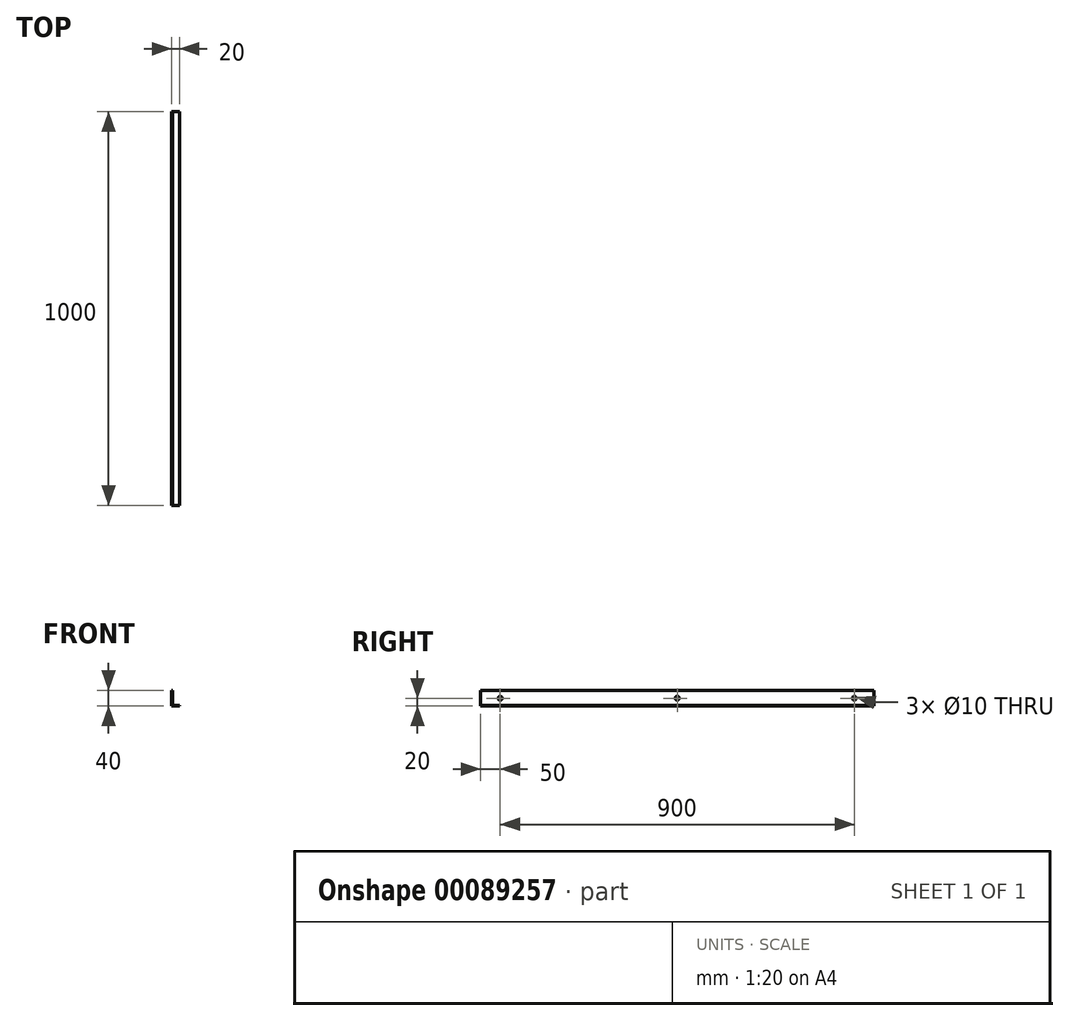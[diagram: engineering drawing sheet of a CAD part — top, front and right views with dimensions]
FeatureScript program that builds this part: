
annotation { "Feature Type Name" : "Feature", "Feature Type Description" : "" }
export const myFeature = defineFeature(function(context is Context, id is Id, definition is map)
    precondition{}
    {
        {
            var Q0;
            Q0=qCreatedBy(makeId("Front.planeOp"),FACE);
            var sketch = newSketch(context, id + "F0", { "sketchPlane" : qUnion([Q0])});
            skLineSegment(sketch, "E0.bottom", {"start": v(-8, 1) * mm, "end": v(10, 1) * mm});
            skLineSegment(sketch, "E0.top", {"start": v(-10, -1) * mm, "end": v(10, -1) * mm});
            skLineSegment(sketch, "E0.left", {"start": v(-10, 1) * mm, "end": v(-10, -1) * mm});
            skLineSegment(sketch, "E0.right", {"start": v(10, 1) * mm, "end": v(10, -1) * mm});
            skPoint(sketch, "E0.middle", {"position": v(0, 0) * mm});
            skLineSegment(sketch, "E1.bottom", {"start": v(-10, -1) * mm, "end": v(-8, -1) * mm});
            skLineSegment(sketch, "E1.top", {"start": v(-10, 39) * mm, "end": v(-8, 39) * mm});
            skLineSegment(sketch, "E1.left", {"start": v(-10, -1) * mm, "end": v(-10, 39) * mm});
            skLineSegment(sketch, "E1.right", {"start": v(-8, 1) * mm, "end": v(-8, 39) * mm});
            skSolve(sketch);
        }
        {
            var Q0;
            Q0 = qSketchRegion(id + "F0", true);
            extrude(context, id + "F1", {"entities" : qUnion([Q0]), "depth" : 1000 * mm});
        }
        {
            var Q0;
            Q0=makeQuery(id+"F1.opExtrude","SWEPT_FACE",FACE,{"disambiguationData":[OSD([sQuery(id+"F0.wireOp",EDGE,"E1.left")])]});
            var sketch = newSketch(context, id + "F2", { "sketchPlane" : qUnion([Q0])});
            skLineSegment(sketch, "E2", {"start": v(0, 19) * mm, "end": v(50, 19) * mm, "construction": true});
            skCircle(sketch, "E3", {"center": v(50, 19) * mm, "radius": 5 * mm});
            skLineSegment(sketch, "E4", {"start": v(1000, 19) * mm, "end": v(950, 19) * mm, "construction": true});
            skCircle(sketch, "E5", {"center": v(950, 19) * mm, "radius": 5 * mm});
            skLineSegment(sketch, "E6", {"start": v(50, 19) * mm, "end": v(950, 19) * mm, "construction": true});
            skCircle(sketch, "E7", {"center": v(500, 19) * mm, "radius": 5 * mm});
            skSolve(sketch);
        }
        {
            var Q0;
            Q0=makeQuery(id+"F2.imprint","IMPRINT",FACE,{"disambiguationData":[TD([[makeQuery(id+"F2.imprint","IMPRINT",EDGE,{"derivedFrom":sQuery(id+"F2.wireOp",EDGE,"E3")}),1.0]])]});
            var Q1;
            Q1=makeQuery(id+"F2.imprint","IMPRINT",FACE,{"disambiguationData":[TD([[makeQuery(id+"F2.imprint","IMPRINT",EDGE,{"derivedFrom":sQuery(id+"F2.wireOp",EDGE,"E5")}),1.0]])]});
            var Q2;
            Q2=makeQuery(id+"F2.imprint","IMPRINT",FACE,{"disambiguationData":[TD([[makeQuery(id+"F2.imprint","IMPRINT",EDGE,{"derivedFrom":sQuery(id+"F2.wireOp",EDGE,"E7")}),1.0]])]});
            var Q3;
            Q3=makeQuery(id+"F2.imprint","IMPRINT",FACE,{"disambiguationData":[TD([[makeQuery(id+"F2.imprint","IMPRINT",EDGE,{"derivedFrom":sQuery(id+"F2.wireOp",EDGE,"E7")}),1.0]])]});
            extrude(context, id + "F3", {"entities" : qUnion([Q0, Q1, Q2, Q3]), "operationType" : NewBodyOperationType.REMOVE, "oppositeDirection" : true, "depth" : 25 * mm});
        }
    });
